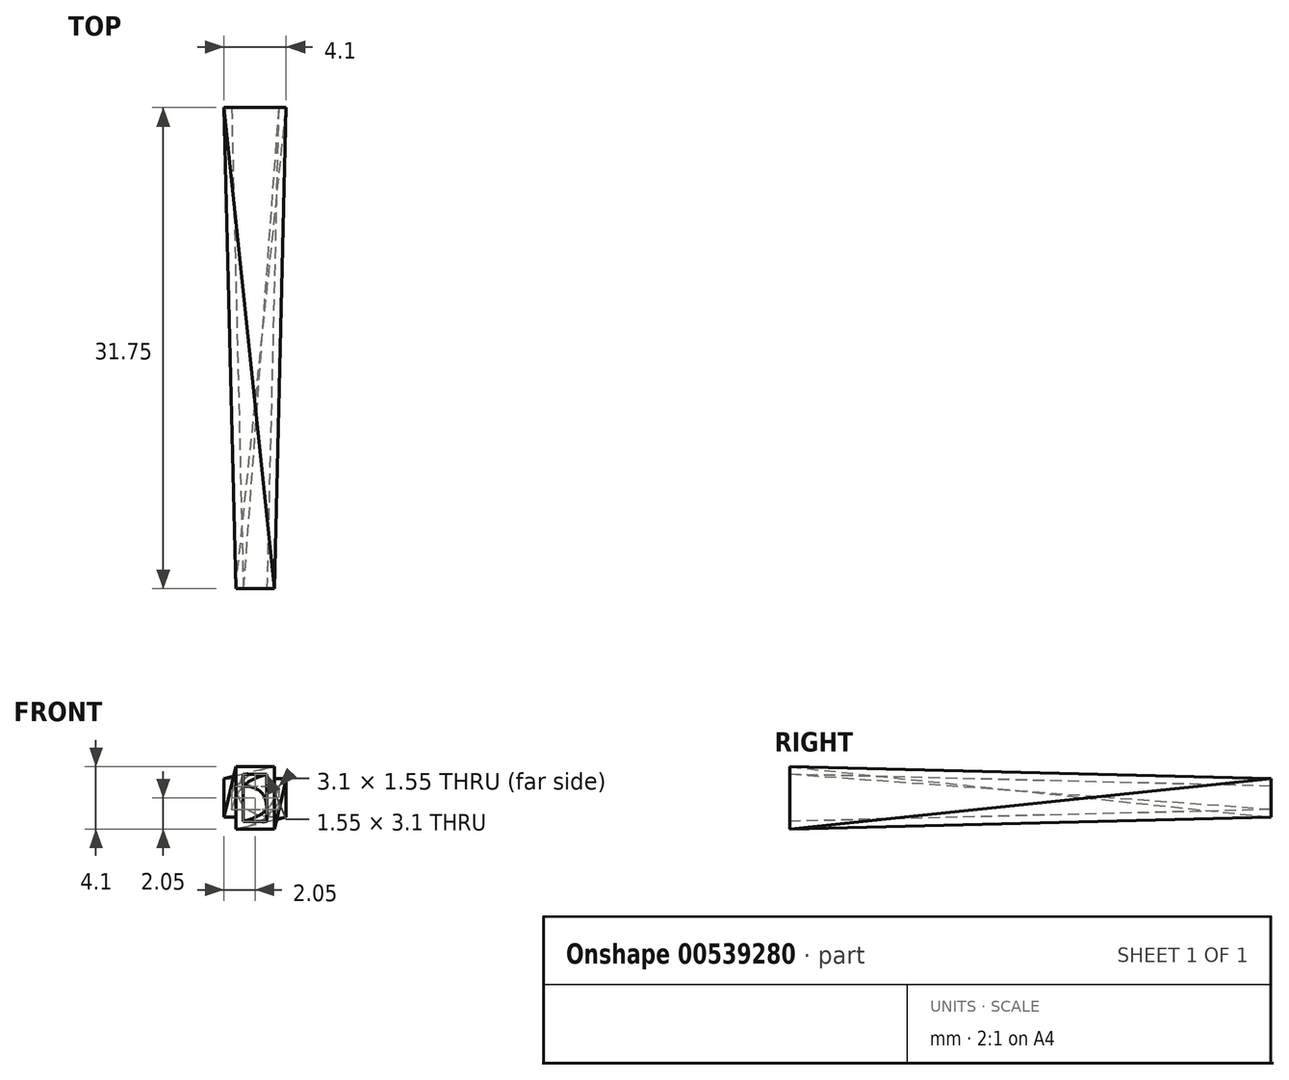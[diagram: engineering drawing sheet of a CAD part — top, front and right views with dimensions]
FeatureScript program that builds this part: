
annotation { "Feature Type Name" : "Feature", "Feature Type Description" : "" }
export const myFeature = defineFeature(function(context is Context, id is Id, definition is map)
    precondition{}
    {
        {
            var Q0;
            Q0=qCreatedBy(makeId("Front.planeOp"),FACE);
            var sketch = newSketch(context, id + "F0", { "sketchPlane" : qUnion([Q0])});
            skPoint(sketch, "E0.middle", {"position": v(0, 0) * mm});
            skLineSegment(sketch, "E1.bottom", {"start": v(-2.05, -1.27) * mm, "end": v(2.05, -1.27) * mm});
            skLineSegment(sketch, "E1.top", {"start": v(-2.05, 1.27) * mm, "end": v(2.05, 1.27) * mm});
            skLineSegment(sketch, "E1.left", {"start": v(-2.05, -1.27) * mm, "end": v(-2.05, 1.27) * mm});
            skLineSegment(sketch, "E1.right", {"start": v(2.05, -1.27) * mm, "end": v(2.05, 1.27) * mm});
            skCircle(sketch, "E2", {"center": v(0, 0) * mm, "radius": 9.53 * mm});
            skSolve(sketch);
        }
        {
            var Q0;
            Q0=qCreatedBy(makeId("Front.planeOp"),FACE);
            cPlane(context, id + "F1", {"entities" : qUnion([Q0]), "cplaneType" : CPlaneType.OFFSET, "offset" : 31.75 * mm, "width" : 150 * mm, "height" : 150 * mm});
        }
        {
            var Q0;
            Q0=qCreatedBy(id+"F1.planeOp",FACE);
            var sketch = newSketch(context, id + "F2", { "sketchPlane" : qUnion([Q0])});
            skLineSegment(sketch, "E3.bottom", {"start": v(-1.27, 2.05) * mm, "end": v(1.28, 2.05) * mm});
            skLineSegment(sketch, "E3.top", {"start": v(-1.28, -2.05) * mm, "end": v(1.27, -2.05) * mm});
            skLineSegment(sketch, "E3.left", {"start": v(-1.27, 2.05) * mm, "end": v(-1.28, -2.05) * mm});
            skLineSegment(sketch, "E3.right", {"start": v(1.28, 2.05) * mm, "end": v(1.27, -2.05) * mm});
            skPoint(sketch, "E3.middle", {"position": v(0, 0) * mm});
            skCircle(sketch, "E4", {"center": v(0, 0) * mm, "radius": 9.53 * mm});
            skSolve(sketch);
        }
        {
            var Q0;
            Q0=qCreatedBy(id+"F1.planeOp",FACE);
            var sketch = newSketch(context, id + "F3", { "sketchPlane" : qUnion([Q0])});
            skLineSegment(sketch, "E5.bottom", {"start": v(-0.77, -1.55) * mm, "end": v(0.77, -1.55) * mm});
            skLineSegment(sketch, "E5.top", {"start": v(-0.78, 1.55) * mm, "end": v(0.77, 1.55) * mm});
            skLineSegment(sketch, "E5.left", {"start": v(-0.78, -1.55) * mm, "end": v(-0.78, 1.55) * mm});
            skLineSegment(sketch, "E5.right", {"start": v(0.78, -1.55) * mm, "end": v(0.77, 1.55) * mm});
            skPoint(sketch, "E5.middle", {"position": v(0, 0) * mm});
            skSolve(sketch);
        }
        {
            var Q0;
            Q0=qCreatedBy(makeId("Front.planeOp"),FACE);
            var sketch = newSketch(context, id + "F4", { "sketchPlane" : qUnion([Q0])});
            skLineSegment(sketch, "E6.bottom", {"start": v(-1.55, 0.78) * mm, "end": v(1.55, 0.78) * mm});
            skLineSegment(sketch, "E6.top", {"start": v(-1.55, -0.78) * mm, "end": v(1.55, -0.78) * mm});
            skLineSegment(sketch, "E6.left", {"start": v(-1.55, 0.78) * mm, "end": v(-1.55, -0.78) * mm});
            skLineSegment(sketch, "E6.right", {"start": v(1.55, 0.78) * mm, "end": v(1.55, -0.78) * mm});
            skPoint(sketch, "E6.middle", {"position": v(0, 0) * mm});
            skSolve(sketch);
        }
        {
            var Q0;
            Q0=makeQuery(id+"F2.imprint","IMPRINT",FACE,{"disambiguationData":[TD([[makeQuery(id+"F2.imprint","IMPRINT",EDGE,{"derivedFrom":sQuery(id+"F2.wireOp",EDGE,"E3.bottom")}),-1.0]])]});
            var Q1;
            Q1=makeQuery(id+"F0.imprint","IMPRINT",FACE,{"disambiguationData":[TD([[makeQuery(id+"F0.imprint","IMPRINT",EDGE,{"derivedFrom":sQuery(id+"F0.wireOp",EDGE,"E1.bottom")}),1.0]])]});
            var Q2;
            Q2=sQuery(id+"F0.wireOp",VERTEX,"E1.left.end");
            var Q3;
            Q3=sQuery(id+"F2.wireOp",VERTEX,"E3.right.start");
            loft(context, id + "F5", {"sheetProfilesArray" : [{ "sheetProfileEntities" : qUnion([Q0]) }, { "sheetProfileEntities" : qUnion([Q1]) }], "matchConnections" : true, "connections" : [{ "connectionEntities" : qUnion([Q2, Q3]), "connectionEdgeQueries" : qUnion([]), "connectionEdgeParameters" : [] }]});
        }
        {
            var Q1;
            Q1=makeQuery(id+"F4.imprint","IMPRINT",FACE,{"disambiguationData":[TD([[makeQuery(id+"F4.imprint","IMPRINT",EDGE,{"derivedFrom":sQuery(id+"F4.wireOp",EDGE,"E6.bottom")}),-1.0]])]});
            var Q2;
            Q2 = qSketchRegion(id + "F3", true);
            var Q3;
            Q3=sQuery(id+"F3.wireOp",VERTEX,"E5.right.end");
            var Q4;
            Q4=sQuery(id+"F4.wireOp",VERTEX,"E6.left.start");
            loft(context, id + "F6", {"operationType" : NewBodyOperationType.REMOVE, "sheetProfilesArray" : [{ "sheetProfileEntities" : qUnion([Q1]) }, { "sheetProfileEntities" : qUnion([Q2]) }], "matchConnections" : true, "connections" : [{ "connectionEntities" : qUnion([Q3, Q4]), "connectionEdgeQueries" : qUnion([]), "connectionEdgeParameters" : [] }]});
        }
    });
